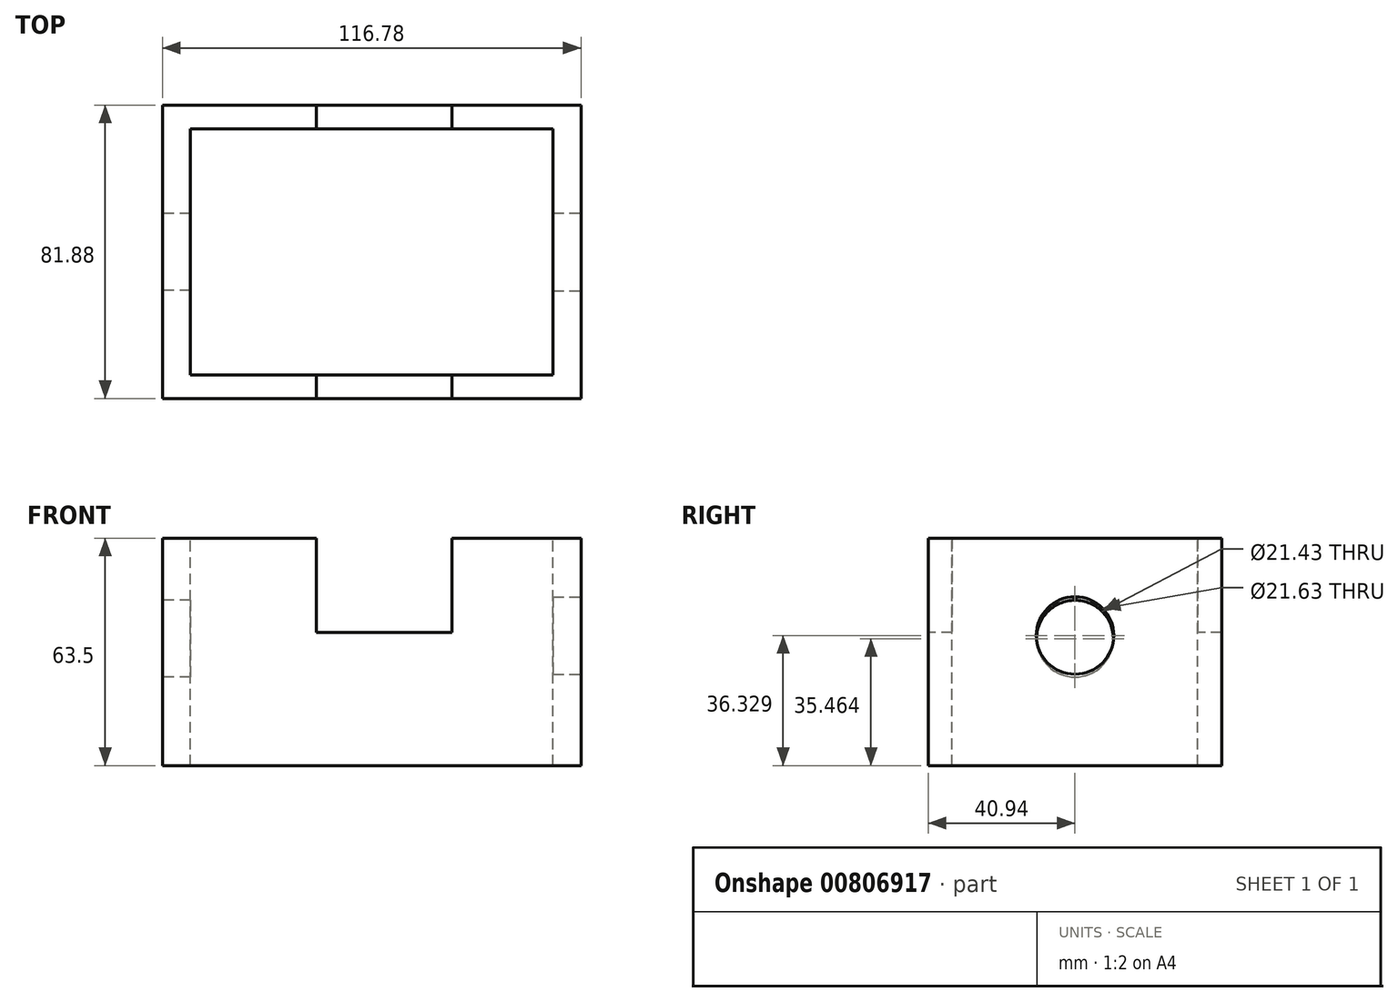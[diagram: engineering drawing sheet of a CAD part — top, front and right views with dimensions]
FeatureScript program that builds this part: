
annotation { "Feature Type Name" : "Feature", "Feature Type Description" : "" }
export const myFeature = defineFeature(function(context is Context, id is Id, definition is map)
    precondition{}
    {
        {
            var Q0;
            Q0=qCreatedBy(makeId("Top.planeOp"),FACE);
            var sketch = newSketch(context, id + "F0", { "sketchPlane" : qUnion([Q0])});
            skLineSegment(sketch, "E0.bottom", {"start": v(-58.39, 40.94) * mm, "end": v(58.39, 40.94) * mm});
            skLineSegment(sketch, "E0.top", {"start": v(-58.39, -40.94) * mm, "end": v(58.39, -40.94) * mm});
            skLineSegment(sketch, "E0.left", {"start": v(-58.39, 40.94) * mm, "end": v(-58.39, -40.94) * mm});
            skLineSegment(sketch, "E0.right", {"start": v(58.39, 40.94) * mm, "end": v(58.39, -40.94) * mm});
            skPoint(sketch, "E0.middle", {"position": v(0, 0) * mm});
            skSolve(sketch);
        }
        {
            var Q0;
            Q0=makeQuery(id+"F0.imprint","IMPRINT",FACE,{"disambiguationData":[TD([[makeQuery(id+"F0.imprint","IMPRINT",EDGE,{"derivedFrom":sQuery(id+"F0.wireOp",EDGE,"E0.bottom")}),-1.0]])]});
            extrude(context, id + "F1", {"entities" : qUnion([Q0]), "depth" : 63.5 * mm, "offsetDistance" : 25.4 * mm});
        }
        {
            var Q0;
            Q0=makeQuery(id+"F1.opExtrude","CAP_FACE",FACE,{"disambiguationData":[OSD([sQuery(id+"F0.wireOp",EDGE,"E0.bottom"),sQuery(id+"F0.wireOp",EDGE,"E0.top"),sQuery(id+"F0.wireOp",EDGE,"E0.left"),sQuery(id+"F0.wireOp",EDGE,"E0.right")])],"isStart":false});
            var sketch = newSketch(context, id + "F2", { "sketchPlane" : qUnion([Q0])});
            skLineSegment(sketch, "E1.bottom", {"start": v(-50.6, 34.31) * mm, "end": v(50.6, 34.31) * mm});
            skLineSegment(sketch, "E1.top", {"start": v(-50.6, -34.31) * mm, "end": v(50.6, -34.31) * mm});
            skLineSegment(sketch, "E1.left", {"start": v(-50.6, 34.31) * mm, "end": v(-50.6, -34.31) * mm});
            skLineSegment(sketch, "E1.right", {"start": v(50.6, 34.31) * mm, "end": v(50.6, -34.31) * mm});
            skPoint(sketch, "E1.middle", {"position": v(0, 0) * mm});
            skSolve(sketch);
        }
        {
            var Q0;
            Q0=makeQuery(id+"F2.imprint","IMPRINT",FACE,{"disambiguationData":[TD([[makeQuery(id+"F2.imprint","IMPRINT",EDGE,{"derivedFrom":sQuery(id+"F2.wireOp",EDGE,"E1.bottom")}),-1.0]])]});
            extrude(context, id + "F3", {"entities" : qUnion([Q0]), "operationType" : NewBodyOperationType.REMOVE, "oppositeDirection" : true, "depth" : 76.2 * mm, "offsetDistance" : 25.4 * mm});
        }
        {
            var Q0;
            Q0=makeQuery(id+"F1.opExtrude","SWEPT_FACE",FACE,{"disambiguationData":[OSD([sQuery(id+"F0.wireOp",EDGE,"E0.top")])]});
            var sketch = newSketch(context, id + "F4", { "sketchPlane" : qUnion([Q0])});
            skLineSegment(sketch, "E2.bottom", {"start": v(-15.43, 63.5) * mm, "end": v(22.35, 63.5) * mm});
            skLineSegment(sketch, "E2.top", {"start": v(-15.43, 37.2) * mm, "end": v(22.35, 37.2) * mm});
            skLineSegment(sketch, "E2.left", {"start": v(-15.43, 63.5) * mm, "end": v(-15.43, 37.2) * mm});
            skLineSegment(sketch, "E2.right", {"start": v(22.35, 63.5) * mm, "end": v(22.35, 37.2) * mm});
            skSolve(sketch);
        }
        {
            var Q0;
            Q0=makeQuery(id+"F4.imprint","IMPRINT",FACE,{"disambiguationData":[TD([[makeQuery(id+"F4.imprint","IMPRINT",EDGE,{"derivedFrom":sQuery(id+"F4.wireOp",EDGE,"E2.bottom")}),-1.0]])]});
            extrude(context, id + "F5", {"entities" : qUnion([Q0]), "operationType" : NewBodyOperationType.REMOVE, "oppositeDirection" : true, "depth" : 101.6 * mm, "offsetDistance" : 25.4 * mm});
        }
        {
            var Q0;
            Q0=makeQuery(id+"F1.opExtrude","SWEPT_FACE",FACE,{"disambiguationData":[OSD([sQuery(id+"F0.wireOp",EDGE,"E0.left")])]});
            var sketch = newSketch(context, id + "F6", { "sketchPlane" : qUnion([Q0])});
            skCircle(sketch, "E3", {"center": v(0, 35.46) * mm, "radius": 10.72 * mm});
            skSolve(sketch);
        }
        {
            var Q0;
            Q0=makeQuery(id+"F6.imprint","IMPRINT",FACE,{"disambiguationData":[TD([[makeQuery(id+"F6.imprint","IMPRINT",EDGE,{"derivedFrom":sQuery(id+"F6.wireOp",EDGE,"E3")}),1.0]])]});
            extrude(context, id + "F7", {"entities" : qUnion([Q0]), "operationType" : NewBodyOperationType.REMOVE, "oppositeDirection" : true, "depth" : 101.6 * mm, "offsetDistance" : 25.4 * mm});
        }
        {
            var Q0;
            Q0=makeQuery(id+"F1.opExtrude","SWEPT_FACE",FACE,{"disambiguationData":[OSD([sQuery(id+"F0.wireOp",EDGE,"E0.right")])]});
            var sketch = newSketch(context, id + "F8", { "sketchPlane" : qUnion([Q0])});
            skCircle(sketch, "E4", {"center": v(0, 36.33) * mm, "radius": 10.82 * mm});
            skSolve(sketch);
        }
        {
            var Q0;
            Q0=makeQuery(id+"F8.imprint","IMPRINT",FACE,{"disambiguationData":[TD([[makeQuery(id+"F8.imprint","IMPRINT",EDGE,{"derivedFrom":sQuery(id+"F8.wireOp",EDGE,"E4")}),1.0]])]});
            extrude(context, id + "F9", {"entities" : qUnion([Q0]), "operationType" : NewBodyOperationType.REMOVE, "oppositeDirection" : true, "depth" : 101.6 * mm, "offsetDistance" : 25.4 * mm});
        }
    });
